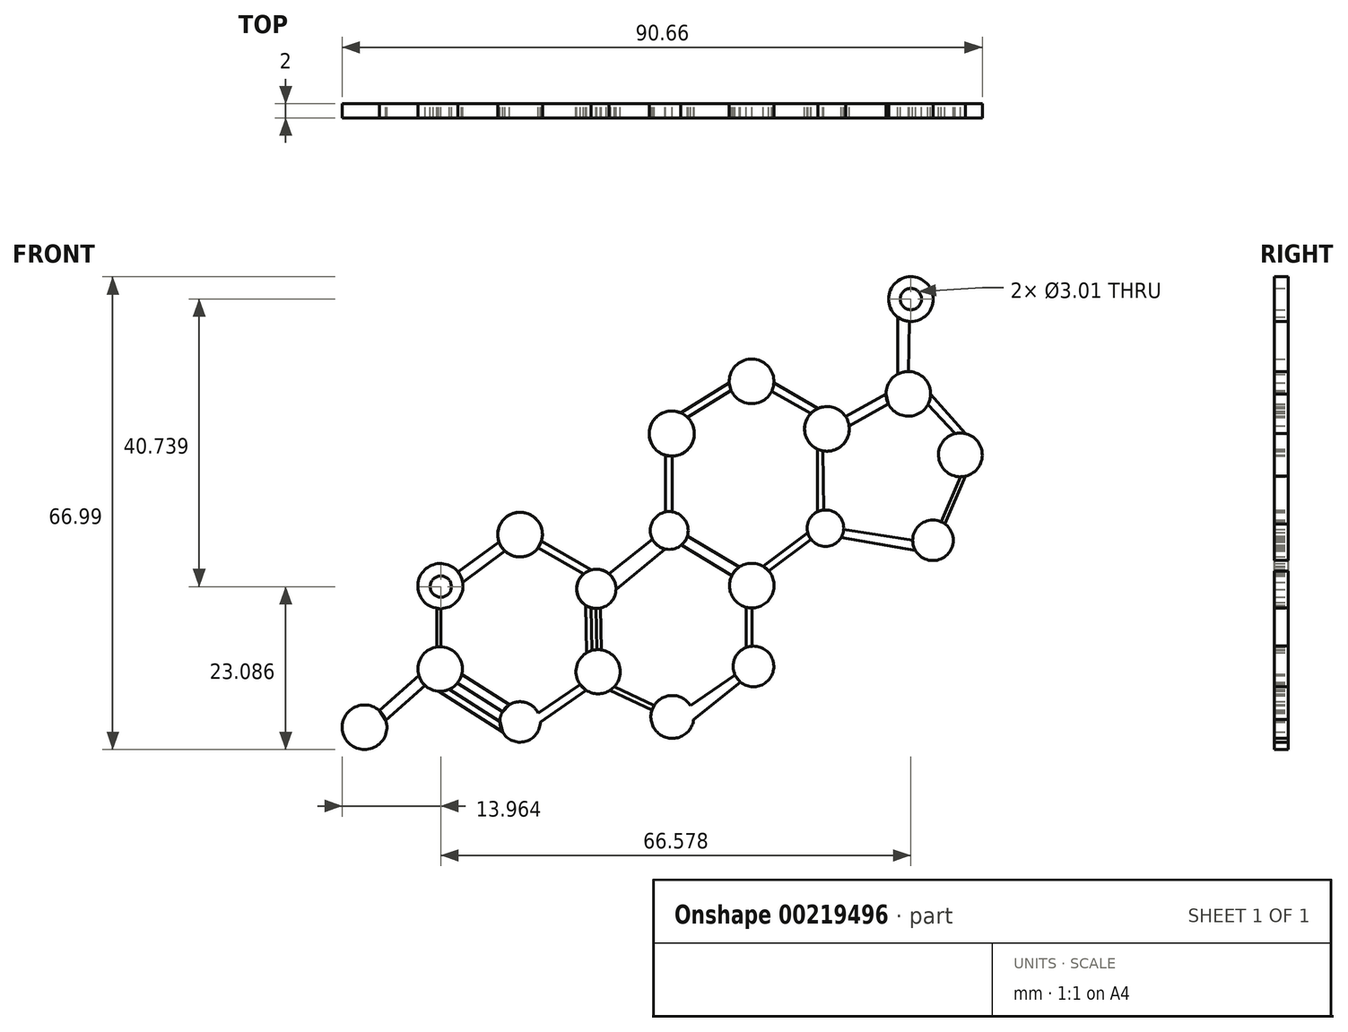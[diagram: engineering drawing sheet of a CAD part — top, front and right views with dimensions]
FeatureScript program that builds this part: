
annotation { "Feature Type Name" : "Feature", "Feature Type Description" : "" }
export const myFeature = defineFeature(function(context is Context, id is Id, definition is map)
    precondition{}
    {
        {
            var Q0;
            Q0=qCreatedBy(makeId("Front.planeOp"),FACE);
            var sketch = newSketch(context, id + "F0", { "sketchPlane" : qUnion([Q0])});
            skCircle(sketch, "E0", {"center": v(-62.79, -30.39) * mm, "radius": 3.16 * mm});
            skCircle(sketch, "E1", {"center": v(-52.09, -22.14) * mm, "radius": 3.15 * mm});
            skCircle(sketch, "E2", {"center": v(-40.76, -29.64) * mm, "radius": 2.86 * mm});
            skCircle(sketch, "E3", {"center": v(-29.71, -22.52) * mm, "radius": 3.13 * mm});
            skCircle(sketch, "E4", {"center": v(-29.95, -10.78) * mm, "radius": 2.78 * mm});
            skCircle(sketch, "E5", {"center": v(-52.05, -10.39) * mm, "radius": 3.2 * mm});
            skCircle(sketch, "E6", {"center": v(-40.75, -3.1) * mm, "radius": 3.16 * mm});
            skCircle(sketch, "E7", {"center": v(-19.19, -28.93) * mm, "radius": 3.04 * mm});
            skCircle(sketch, "E8", {"center": v(-7.7, -21.77) * mm, "radius": 2.88 * mm});
            skCircle(sketch, "E9", {"center": v(-7.93, -10.32) * mm, "radius": 3.16 * mm});
            skCircle(sketch, "E10", {"center": v(-19.63, -2.51) * mm, "radius": 2.68 * mm});
            skCircle(sketch, "E11", {"center": v(2.5, -2.18) * mm, "radius": 2.58 * mm});
            skCircle(sketch, "E12", {"center": v(2.7, 11.88) * mm, "radius": 3.16 * mm});
            skCircle(sketch, "E13", {"center": v(-19.27, 11.22) * mm, "radius": 3.2 * mm});
            skCircle(sketch, "E14", {"center": v(-7.96, 18.61) * mm, "radius": 3.16 * mm});
            skCircle(sketch, "E15", {"center": v(17.72, -3.9) * mm, "radius": 2.87 * mm});
            skCircle(sketch, "E16", {"center": v(21.6, 8.2) * mm, "radius": 3.1 * mm});
            skCircle(sketch, "E17", {"center": v(14.23, 16.85) * mm, "radius": 3.16 * mm});
            skCircle(sketch, "E18", {"center": v(14.6, 30.28) * mm, "radius": 3.16 * mm});
            skLineSegment(sketch, "E19", {"start": v(-51.95, -13.58) * mm, "end": v(-51.95, -18.99) * mm});
            skLineSegment(sketch, "E20", {"start": v(-37.9, -29.64) * mm, "end": v(-31.39, -25.16) * mm});
            skLineSegment(sketch, "E21", {"start": v(-38.2, -4.96) * mm, "end": v(-31.76, -8.67) * mm});
            skLineSegment(sketch, "E22", {"start": v(-28.14, -8.67) * mm, "end": v(-22, -3.76) * mm});
            skLineSegment(sketch, "E23", {"start": v(-7.93, -13.48) * mm, "end": v(-7.93, -18.9) * mm});
            skLineSegment(sketch, "E24", {"start": v(-9.53, -23.99) * mm, "end": v(-16.17, -29.29) * mm});
            skLineSegment(sketch, "E25", {"start": v(-28.04, -25.16) * mm, "end": v(-22.06, -27.94) * mm});
            skLineSegment(sketch, "E26", {"start": v(-19.23, 8.02) * mm, "end": v(-19.23, 0.14) * mm});
            skLineSegment(sketch, "E27", {"start": v(-17.07, 13.53) * mm, "end": v(-10.86, 17.34) * mm});
            skLineSegment(sketch, "E28", {"start": v(-6.33, -7.59) * mm, "end": v(0, -2.8) * mm});
            skLineSegment(sketch, "E29", {"start": v(2.14, 8.77) * mm, "end": v(2.27, 0.39) * mm});
            skLineSegment(sketch, "E30", {"start": v(5.34, 13.63) * mm, "end": v(11.06, 16.85) * mm});
            skLineSegment(sketch, "E31", {"start": v(17.01, 15.35) * mm, "end": v(20.88, 11.22) * mm});
            skLineSegment(sketch, "E32", {"start": v(14.36, 27.12) * mm, "end": v(14.23, 20.01) * mm});
            skLineSegment(sketch, "E33", {"start": v(5.07, -2.37) * mm, "end": v(14.85, -3.9) * mm});
            skLineSegment(sketch, "E34", {"start": v(21.6, 5.1) * mm, "end": v(18.87, -1.27) * mm});
            skLineSegment(sketch, "E35", {"start": v(-50.79, -25) * mm, "end": v(-43.62, -29.58) * mm});
            skLineSegment(sketch, "E36", {"start": v(-49.64, -24.12) * mm, "end": v(-43.24, -28.2) * mm});
            skLineSegment(sketch, "E37", {"start": v(-48.9, -9.85) * mm, "end": v(-42.9, -5.42) * mm});
            skPoint(sketch, "E38.startSnap0", {"position": v(-45.9, -7.63) * mm});
            skLineSegment(sketch, "E39", {"start": v(-49.54, -8.4) * mm, "end": v(-43.75, -4.12) * mm});
            skLineSegment(sketch, "E40", {"start": v(-59.78, -29.4) * mm, "end": v(-54.2, -24.48) * mm});
            skLineSegment(sketch, "E41", {"start": v(-55.1, -23.07) * mm, "end": v(-60.7, -28.01) * mm});
            skLineSegment(sketch, "E42", {"start": v(-59.78, -29.4) * mm, "end": v(-60.7, -28.01) * mm});
            skLineSegment(sketch, "E43", {"start": v(12.7, 19.62) * mm, "end": v(12.7, 27.74) * mm});
            skLineSegment(sketch, "E44", {"start": v(-28.56, -13.19) * mm, "end": v(-27.93, -12.7) * mm});
            skLineSegment(sketch, "E45", {"start": v(-43.24, -28.2) * mm, "end": v(-42.27, -27.2) * mm});
            skLineSegment(sketch, "E46", {"start": v(-42.27, -27.2) * mm, "end": v(-49.03, -22.9) * mm});
            skLineSegment(sketch, "E47", {"start": v(-43.24, -31.06) * mm, "end": v(-52.3, -25.28) * mm});
            skLineSegment(sketch, "E48", {"start": v(-43.62, -29.58) * mm, "end": v(-43.24, -31.06) * mm});
            skLineSegment(sketch, "E49", {"start": v(-38.17, -28.41) * mm, "end": v(-32.25, -24.35) * mm});
            skLineSegment(sketch, "E50", {"start": v(-31.39, -25.16) * mm, "end": v(-32.25, -24.35) * mm});
            skLineSegment(sketch, "E51", {"start": v(-21.76, -27.3) * mm, "end": v(-27.43, -24.67) * mm});
            skLineSegment(sketch, "E52", {"start": v(-28.04, -25.16) * mm, "end": v(-27.43, -24.67) * mm});
            skLineSegment(sketch, "E53", {"start": v(-21.76, -27.3) * mm, "end": v(-22.06, -27.94) * mm});
            skLineSegment(sketch, "E54", {"start": v(-16.6, -27.32) * mm, "end": v(-10.3, -23) * mm});
            skLineSegment(sketch, "E55", {"start": v(-10.3, -23) * mm, "end": v(-9.53, -23.99) * mm});
            skLineSegment(sketch, "E56", {"start": v(-8.73, -19.09) * mm, "end": v(-8.73, -13.38) * mm});
            skLineSegment(sketch, "E57", {"start": v(-8.73, -13.38) * mm, "end": v(-7.93, -13.48) * mm});
            skLineSegment(sketch, "E58", {"start": v(-8.73, -19.09) * mm, "end": v(-7.93, -18.9) * mm});
            skLineSegment(sketch, "E59", {"start": v(-5.53, -8.26) * mm, "end": v(0.45, -3.75) * mm});
            skLineSegment(sketch, "E60", {"start": v(-5.53, -8.26) * mm, "end": v(-6.33, -7.59) * mm});
            skLineSegment(sketch, "E61", {"start": v(-51.95, -13.58) * mm, "end": v(-53.08, -13.4) * mm});
            skLineSegment(sketch, "E62", {"start": v(-37.73, -4.04) * mm, "end": v(-30.68, -8.1) * mm});
            skLineSegment(sketch, "E63", {"start": v(-31.76, -8.67) * mm, "end": v(-38.2, -4.96) * mm});
            skLineSegment(sketch, "E64", {"start": v(-37.73, -4.04) * mm, "end": v(-38.2, -4.96) * mm});
            skLineSegment(sketch, "E65", {"start": v(-20.17, 8.15) * mm, "end": v(-20.17, 0.14) * mm});
            skLineSegment(sketch, "E66", {"start": v(-20.17, 0.14) * mm, "end": v(-19.8, 0.16) * mm});
            skLineSegment(sketch, "E67", {"start": v(-20.17, 8.15) * mm, "end": v(-19.23, 8.02) * mm});
            skLineSegment(sketch, "E68", {"start": v(-18.04, 14.17) * mm, "end": v(-11.12, 18.41) * mm});
            skLineSegment(sketch, "E69", {"start": v(-11.12, 18.41) * mm, "end": v(-10.86, 17.34) * mm});
            skLineSegment(sketch, "E70", {"start": v(1.37, 9.01) * mm, "end": v(1.37, 0.14) * mm});
            skLineSegment(sketch, "E71", {"start": v(2.14, 8.77) * mm, "end": v(1.37, 9.01) * mm});
            skLineSegment(sketch, "E72", {"start": v(5.84, 12.29) * mm, "end": v(11.4, 15.41) * mm});
            skLineSegment(sketch, "E73", {"start": v(11.4, 15.41) * mm, "end": v(11.06, 16.85) * mm});
            skLineSegment(sketch, "E74", {"start": v(17.4, 16.85) * mm, "end": v(22.33, 11.22) * mm});
            skPoint(sketch, "E75.endSnap0", {"position": v(19.86, 14.03) * mm});
            skLineSegment(sketch, "E76", {"start": v(21.6, 5.1) * mm, "end": v(22.33, 5.18) * mm});
            skLineSegment(sketch, "E77", {"start": v(4.7, -3.53) * mm, "end": v(15.24, -5.35) * mm});
            skLineSegment(sketch, "E78", {"start": v(-27.17, -10.89) * mm, "end": v(-20.2, -5.13) * mm});
            skLineSegment(sketch, "E79", {"start": v(-17.9, -4.57) * mm, "end": v(-10.75, -8.87) * mm});
            skLineSegment(sketch, "E80", {"start": v(-17.06, -3.28) * mm, "end": v(-9.71, -7.7) * mm});
            skLineSegment(sketch, "E81", {"start": v(-31.47, -13.1) * mm, "end": v(-31.32, -19.84) * mm});
            skLineSegment(sketch, "E82", {"start": v(-30.68, -13.47) * mm, "end": v(-30.59, -19.52) * mm});
            skLineSegment(sketch, "E83", {"start": v(-29.98, -13.56) * mm, "end": v(-29.89, -19.4) * mm});
            skLineSegment(sketch, "E84", {"start": v(-29.35, -13.5) * mm, "end": v(-29.26, -19.42) * mm});
            skLineSegment(sketch, "E85", {"start": v(-52.51, -13.5) * mm, "end": v(-52.51, -19.01) * mm});
            skLineSegment(sketch, "E86", {"start": v(-4.8, 18.43) * mm, "end": v(1.41, 14.77) * mm});
            skLineSegment(sketch, "E87", {"start": v(-5.3, 17.28) * mm, "end": v(0.43, 14.07) * mm});
            skLineSegment(sketch, "E88", {"start": v(22.33, 5.18) * mm, "end": v(19.43, -1.59) * mm});
            skCircle(sketch, "E89", {"center": v(14.6, 30.28) * mm, "radius": 1.5 * mm});
            skCircle(sketch, "E90", {"center": v(-51.99, -10.46) * mm, "radius": 1.5 * mm});
            skSolve(sketch);
        }
        {
            var Q0;
            {var subQ3=sQuery(id+"F0.wireOp",EDGE,"E64");Q0=makeQuery(id+"F0.imprint","IMPRINT",FACE,{"disambiguationData":[TD([[makeQuery(id+"F0.imprint","IMPRINT",EDGE,{"derivedFrom":subQ3}),-1.0]])]});}
            var Q1;
            {var subQ0=sQuery(id+"F0.wireOp",EDGE,"Mb7MF2RT-jddo-B6ze-xgIj-n0XcXyZHC1Ex");Q1=makeQuery(id+"F0.imprint","IMPRINT",FACE,{"disambiguationData":[TD([[makeQuery(id+"F0.imprint","IMPRINT",EDGE,{"derivedFrom":subQ0}),1.0]])]});}
            var Q2;
            {var subQ1=sQuery(id+"F0.wireOp",EDGE,"E37");Q2=makeQuery(id+"F0.imprint","IMPRINT",FACE,{"disambiguationData":[TD([[makeQuery(id+"F0.imprint","IMPRINT",EDGE,{"derivedFrom":subQ1}),1.0]])]});}
            var Q3;
            {var subQ1=sQuery(id+"F0.wireOp",EDGE,"E19");Q3=makeQuery(id+"F0.imprint","IMPRINT",FACE,{"disambiguationData":[TD([[makeQuery(id+"F0.imprint","IMPRINT",EDGE,{"derivedFrom":subQ1}),-1.0]])]});}
            var Q4;
            {var subQ5=sQuery(id+"F0.wireOp",EDGE,"a1dBgSWb-6DuU-worO-kKtV-IeXW11xfBRhP");Q4=makeQuery(id+"F0.imprint","IMPRINT",FACE,{"disambiguationData":[TD([[makeQuery(id+"F0.imprint","IMPRINT",EDGE,{"derivedFrom":subQ5}),-1.0]])]});}
            var Q5;
            {var subQ1=sQuery(id+"F0.wireOp",EDGE,"E40");Q5=makeQuery(id+"F0.imprint","IMPRINT",FACE,{"disambiguationData":[TD([[makeQuery(id+"F0.imprint","IMPRINT",EDGE,{"derivedFrom":subQ1}),1.0]])]});}
            var Q6;
            {var subQ0=sQuery(id+"F0.wireOp",EDGE,"E42");Q6=makeQuery(id+"F0.imprint","IMPRINT",FACE,{"disambiguationData":[TD([[makeQuery(id+"F0.imprint","IMPRINT",EDGE,{"derivedFrom":subQ0}),1.0]])]});}
            var Q7;
            {var subQ1=sQuery(id+"F0.wireOp",EDGE,"E36");Q7=makeQuery(id+"F0.imprint","IMPRINT",FACE,{"disambiguationData":[TD([[makeQuery(id+"F0.imprint","IMPRINT",EDGE,{"derivedFrom":subQ1}),1.0]])]});}
            var Q8;
            {var subQ1=sQuery(id+"F0.wireOp",EDGE,"E35");Q8=makeQuery(id+"F0.imprint","IMPRINT",FACE,{"disambiguationData":[TD([[makeQuery(id+"F0.imprint","IMPRINT",EDGE,{"derivedFrom":subQ1}),-1.0]])]});}
            var Q9;
            {var subQ1=sQuery(id+"F0.wireOp",EDGE,"E20");Q9=makeQuery(id+"F0.imprint","IMPRINT",FACE,{"disambiguationData":[TD([[makeQuery(id+"F0.imprint","IMPRINT",EDGE,{"derivedFrom":subQ1}),1.0]])]});}
            var Q10;
            {var subQ3=sQuery(id+"F0.wireOp",EDGE,"E45");Q10=makeQuery(id+"F0.imprint","IMPRINT",FACE,{"disambiguationData":[TD([[makeQuery(id+"F0.imprint","IMPRINT",EDGE,{"derivedFrom":subQ3}),-1.0]])]});}
            var Q11;
            {var subQ0=sQuery(id+"F0.wireOp",EDGE,"E50");Q11=makeQuery(id+"F0.imprint","IMPRINT",FACE,{"disambiguationData":[TD([[makeQuery(id+"F0.imprint","IMPRINT",EDGE,{"derivedFrom":subQ0}),-1.0]])]});}
            var Q12;
            Q12=makeQuery(id+"F0.imprint","IMPRINT",FACE,{"disambiguationData":[TD([[makeQuery(id+"F0.imprint","IMPRINT",EDGE,{"derivedFrom":sQuery(id+"F0.wireOp",EDGE,"5VwYfp6s-fnZS-L74V-JAx9-Tji8LIlleJzu.bottom")}),-1.0]])]});
            var Q13;
            {var subQ5=sQuery(id+"F0.wireOp",EDGE,"M7uNgQcp-6DOX-0CdO-FolA-AVuqSKqm1bxD.bottom");Q13=makeQuery(id+"F0.imprint","IMPRINT",FACE,{"disambiguationData":[TD([[makeQuery(id+"F0.imprint","IMPRINT",EDGE,{"derivedFrom":subQ5}),-1.0]])]});}
            var Q14;
            {var subQ0=sQuery(id+"F0.wireOp",EDGE,"E44");Q14=makeQuery(id+"F0.imprint","IMPRINT",FACE,{"disambiguationData":[TD([[makeQuery(id+"F0.imprint","IMPRINT",EDGE,{"derivedFrom":subQ0}),1.0]])]});}
            var Q15;
            {var subQ0=sQuery(id+"F0.wireOp",EDGE,"E62");Q15=makeQuery(id+"F0.imprint","IMPRINT",FACE,{"disambiguationData":[TD([[makeQuery(id+"F0.imprint","IMPRINT",EDGE,{"derivedFrom":subQ0}),-1.0]])]});}
            var Q16;
            {var subQ1=sQuery(id+"F0.wireOp",EDGE,"E22");Q16=makeQuery(id+"F0.imprint","IMPRINT",FACE,{"disambiguationData":[TD([[makeQuery(id+"F0.imprint","IMPRINT",EDGE,{"derivedFrom":subQ1}),-1.0]])]});}
            var Q17;
            {var subQ0=sQuery(id+"F0.wireOp",EDGE,"UeHGOHKe-4UKH-cGRf-4B86-QE9oBGHCOTL0");Q17=makeQuery(id+"F0.imprint","IMPRINT",FACE,{"disambiguationData":[TD([[makeQuery(id+"F0.imprint","IMPRINT",EDGE,{"derivedFrom":subQ0}),1.0]])]});}
            var Q18;
            {var subQ1=sQuery(id+"F0.wireOp",EDGE,"E25");Q18=makeQuery(id+"F0.imprint","IMPRINT",FACE,{"disambiguationData":[TD([[makeQuery(id+"F0.imprint","IMPRINT",EDGE,{"derivedFrom":subQ1}),1.0]])]});}
            var Q19;
            {var subQ0=sQuery(id+"F0.wireOp",EDGE,"E53");Q19=makeQuery(id+"F0.imprint","IMPRINT",FACE,{"disambiguationData":[TD([[makeQuery(id+"F0.imprint","IMPRINT",EDGE,{"derivedFrom":subQ0}),1.0]])]});}
            var Q20;
            {var subQ1=sQuery(id+"F0.wireOp",EDGE,"E24");Q20=makeQuery(id+"F0.imprint","IMPRINT",FACE,{"disambiguationData":[TD([[makeQuery(id+"F0.imprint","IMPRINT",EDGE,{"derivedFrom":subQ1}),-1.0]])]});}
            var Q21;
            {var subQ0=sQuery(id+"F0.wireOp",EDGE,"E55");Q21=makeQuery(id+"F0.imprint","IMPRINT",FACE,{"disambiguationData":[TD([[makeQuery(id+"F0.imprint","IMPRINT",EDGE,{"derivedFrom":subQ0}),1.0]])]});}
            var Q22;
            {var subQ1=sQuery(id+"F0.wireOp",EDGE,"E23");Q22=makeQuery(id+"F0.imprint","IMPRINT",FACE,{"disambiguationData":[TD([[makeQuery(id+"F0.imprint","IMPRINT",EDGE,{"derivedFrom":subQ1}),-1.0]])]});}
            var Q23;
            {var subQ0=sQuery(id+"F0.wireOp",EDGE,"E57");Q23=makeQuery(id+"F0.imprint","IMPRINT",FACE,{"disambiguationData":[TD([[makeQuery(id+"F0.imprint","IMPRINT",EDGE,{"derivedFrom":subQ0}),1.0]])]});}
            var Q24;
            {var subQ1=sQuery(id+"F0.wireOp",EDGE,"E28");Q24=makeQuery(id+"F0.imprint","IMPRINT",FACE,{"disambiguationData":[TD([[makeQuery(id+"F0.imprint","IMPRINT",EDGE,{"derivedFrom":subQ1}),-1.0]])]});}
            var Q25;
            {var subQ0=sQuery(id+"F0.wireOp",EDGE,"Ezyj9Kgh-BWDU-0eJ4-APll-MsjRslF86DpF");Q25=makeQuery(id+"F0.imprint","IMPRINT",FACE,{"disambiguationData":[TD([[makeQuery(id+"F0.imprint","IMPRINT",EDGE,{"derivedFrom":subQ0}),-1.0]])]});}
            var Q26;
            {var subQ1=sQuery(id+"F0.wireOp",EDGE,"E29");Q26=makeQuery(id+"F0.imprint","IMPRINT",FACE,{"disambiguationData":[TD([[makeQuery(id+"F0.imprint","IMPRINT",EDGE,{"derivedFrom":subQ1}),-1.0]])]});}
            var Q27;
            {var subQ0=sQuery(id+"F0.wireOp",EDGE,"E71");Q27=makeQuery(id+"F0.imprint","IMPRINT",FACE,{"disambiguationData":[TD([[makeQuery(id+"F0.imprint","IMPRINT",EDGE,{"derivedFrom":subQ0}),-1.0]])]});}
            var Q28;
            {var subQ0=sQuery(id+"F0.wireOp",EDGE,"sSouhH1C-a7Wg-rKGi-7Wp8-vkzoGwjJmSID");Q28=makeQuery(id+"F0.imprint","IMPRINT",FACE,{"disambiguationData":[TD([[makeQuery(id+"F0.imprint","IMPRINT",EDGE,{"derivedFrom":subQ0}),-1.0]])]});}
            var Q29;
            {var subQ1=sQuery(id+"F0.wireOp",EDGE,"vSaMkwXp-oE9S-KJV4-mMeU-YnlZ7d6mE9Y9");Q29=makeQuery(id+"F0.imprint","IMPRINT",FACE,{"disambiguationData":[TD([[makeQuery(id+"F0.imprint","IMPRINT",EDGE,{"derivedFrom":subQ1}),-1.0]])]});}
            var Q30;
            {var subQ0=sQuery(id+"F0.wireOp",EDGE,"E68");Q30=makeQuery(id+"F0.imprint","IMPRINT",FACE,{"disambiguationData":[TD([[makeQuery(id+"F0.imprint","IMPRINT",EDGE,{"derivedFrom":subQ0}),-1.0]])]});}
            var Q31;
            {var subQ0=sQuery(id+"F0.wireOp",EDGE,"E67");Q31=makeQuery(id+"F0.imprint","IMPRINT",FACE,{"disambiguationData":[TD([[makeQuery(id+"F0.imprint","IMPRINT",EDGE,{"derivedFrom":subQ0}),1.0]])]});}
            var Q32;
            {var subQ4=sQuery(id+"F0.wireOp",EDGE,"E65");Q32=makeQuery(id+"F0.imprint","IMPRINT",FACE,{"disambiguationData":[TD([[makeQuery(id+"F0.imprint","IMPRINT",EDGE,{"derivedFrom":subQ4}),1.0]])]});}
            var Q33;
            {var subQ1=sQuery(id+"F0.wireOp",EDGE,"E30");Q33=makeQuery(id+"F0.imprint","IMPRINT",FACE,{"disambiguationData":[TD([[makeQuery(id+"F0.imprint","IMPRINT",EDGE,{"derivedFrom":subQ1}),-1.0]])]});}
            var Q34;
            {var subQ1=sQuery(id+"F0.wireOp",EDGE,"E32");Q34=makeQuery(id+"F0.imprint","IMPRINT",FACE,{"disambiguationData":[TD([[makeQuery(id+"F0.imprint","IMPRINT",EDGE,{"derivedFrom":subQ1}),-1.0]])]});}
            var Q35;
            {var subQ0=sQuery(id+"F0.wireOp",EDGE,"sPN0vxyv-kXMr-WsTe-n2yW-GJKV4UbPOXA4");Q35=makeQuery(id+"F0.imprint","IMPRINT",FACE,{"disambiguationData":[TD([[makeQuery(id+"F0.imprint","IMPRINT",EDGE,{"derivedFrom":subQ0}),-1.0]])]});}
            var Q36;
            {var subQ0=sQuery(id+"F0.wireOp",EDGE,"IRrBQA8b-qcgg-vGCc-qcpc-6L5ACvAlk9N0");Q36=makeQuery(id+"F0.imprint","IMPRINT",FACE,{"disambiguationData":[TD([[makeQuery(id+"F0.imprint","IMPRINT",EDGE,{"derivedFrom":subQ0}),-1.0]])]});}
            var Q37;
            {var subQ1=sQuery(id+"F0.wireOp",EDGE,"E31");Q37=makeQuery(id+"F0.imprint","IMPRINT",FACE,{"disambiguationData":[TD([[makeQuery(id+"F0.imprint","IMPRINT",EDGE,{"derivedFrom":subQ1}),1.0]])]});}
            var Q38;
            {var subQ0=sQuery(id+"F0.wireOp",EDGE,"uFY3qbvF-FtAH-bahm-cErt-nJcObRJHhIVn");Q38=makeQuery(id+"F0.imprint","IMPRINT",FACE,{"disambiguationData":[TD([[makeQuery(id+"F0.imprint","IMPRINT",EDGE,{"derivedFrom":subQ0}),1.0]])]});}
            var Q39;
            {var subQ1=sQuery(id+"F0.wireOp",EDGE,"E34");Q39=makeQuery(id+"F0.imprint","IMPRINT",FACE,{"disambiguationData":[TD([[makeQuery(id+"F0.imprint","IMPRINT",EDGE,{"derivedFrom":subQ1}),1.0]])]});}
            var Q40;
            {var subQ0=sQuery(id+"F0.wireOp",EDGE,"sUYJAU2J-VXak-0DQV-njkR-GLYZazPf4Nhu");Q40=makeQuery(id+"F0.imprint","IMPRINT",FACE,{"disambiguationData":[TD([[makeQuery(id+"F0.imprint","IMPRINT",EDGE,{"derivedFrom":subQ0}),-1.0]])]});}
            var Q41;
            {var subQ1=sQuery(id+"F0.wireOp",EDGE,"E33");Q41=makeQuery(id+"F0.imprint","IMPRINT",FACE,{"disambiguationData":[TD([[makeQuery(id+"F0.imprint","IMPRINT",EDGE,{"derivedFrom":subQ1}),-1.0]])]});}
            extrude(context, id + "F1", {"entities" : qUnion([Q0, Q1, Q2, Q3, Q4, Q5, Q6, Q7, Q8, Q9, Q10, Q11, Q12, Q13, Q14, Q15, Q16, Q17, Q18, Q19, Q20, Q21, Q22, Q23, Q24, Q25, Q26, Q27, Q28, Q29, Q30, Q31, Q32, Q33, Q34, Q35, Q36, Q37, Q38, Q39, Q40, Q41]), "depth" : 2 * mm});
        }
        {
            var Q0;
            {var subQ1=sQuery(id+"F0.wireOp",EDGE,"E79");Q0=makeQuery(id+"F0.imprint","IMPRINT",FACE,{"disambiguationData":[TD([[makeQuery(id+"F0.imprint","IMPRINT",EDGE,{"derivedFrom":subQ1}),1.0]])]});}
            extrude(context, id + "F2", {"entities" : qUnion([Q0]), "depth" : 2 * mm});
        }
        {
            var Q0;
            {var subQ1=sQuery(id+"F0.wireOp",EDGE,"E22");Q0=makeQuery(id+"F0.imprint","IMPRINT",FACE,{"disambiguationData":[TD([[makeQuery(id+"F0.imprint","IMPRINT",EDGE,{"derivedFrom":subQ1}),-1.0]])]});}
            extrude(context, id + "F3", {"entities" : qUnion([Q0]), "depth" : 2 * mm});
        }
        {
            var Q0;
            {var subQ0=sQuery(id+"F0.wireOp",EDGE,"E81");Q0=makeQuery(id+"F0.imprint","IMPRINT",FACE,{"disambiguationData":[TD([[makeQuery(id+"F0.imprint","IMPRINT",EDGE,{"derivedFrom":subQ0}),1.0]])]});}
            extrude(context, id + "F4", {"entities" : qUnion([Q0]), "depth" : 2 * mm});
        }
        {
            var Q0;
            {var subQ0=sQuery(id+"F0.wireOp",EDGE,"E22");Q0=makeQuery(id+"F0.imprint","IMPRINT",FACE,{"disambiguationData":[TD([[makeQuery(id+"F0.imprint","IMPRINT",EDGE,{"derivedFrom":subQ0}),-1.0]])]});}
            var Q1;
            {var subQ0=sQuery(id+"F0.wireOp",EDGE,"E83");Q1=makeQuery(id+"F0.imprint","IMPRINT",FACE,{"disambiguationData":[TD([[makeQuery(id+"F0.imprint","IMPRINT",EDGE,{"derivedFrom":subQ0}),1.0]])]});}
            extrude(context, id + "F5", {"entities" : qUnion([Q0, Q1]), "depth" : 2 * mm});
        }
        {
            var Q0;
            {var subQ3=sQuery(id+"F0.wireOp",EDGE,"E64");Q0=makeQuery(id+"F0.imprint","IMPRINT",FACE,{"disambiguationData":[TD([[makeQuery(id+"F0.imprint","IMPRINT",EDGE,{"derivedFrom":subQ3}),-1.0]])]});}
            var Q1;
            {var subQ1=sQuery(id+"F0.wireOp",EDGE,"E5");var subQ4=makeQuery(id+"F0.imprint","INTERSECT",VERTEX,{"derivedFrom":[subQ1,sQuery(id+"F0.wireOp",EDGE,"E37")]});Q1=makeQuery(id+"F0.imprint","IMPRINT",FACE,{"disambiguationData":[TD([[makeQuery(id+"F0.imprint","IMPRINT",EDGE,{"disambiguationData":[TD([[subQ4,-1.0]])],"derivedFrom":subQ1}),1.0]])]});}
            var Q2;
            {var subQ7=sQuery(id+"F0.wireOp",EDGE,"E44");Q2=makeQuery(id+"F0.imprint","IMPRINT",FACE,{"disambiguationData":[TD([[makeQuery(id+"F0.imprint","IMPRINT",EDGE,{"derivedFrom":subQ7}),1.0]])]});}
            var Q3;
            {var subQ0=sQuery(id+"F0.wireOp",EDGE,"E22");Q3=makeQuery(id+"F0.imprint","IMPRINT",FACE,{"disambiguationData":[TD([[makeQuery(id+"F0.imprint","IMPRINT",EDGE,{"derivedFrom":subQ0}),-1.0]])]});}
            var Q4;
            {var subQ3=sQuery(id+"F0.wireOp",EDGE,"E67");Q4=makeQuery(id+"F0.imprint","IMPRINT",FACE,{"disambiguationData":[TD([[makeQuery(id+"F0.imprint","IMPRINT",EDGE,{"derivedFrom":subQ3}),1.0]])]});}
            var Q5;
            {var subQ0=sQuery(id+"F0.wireOp",EDGE,"E69");Q5=makeQuery(id+"F0.imprint","IMPRINT",FACE,{"disambiguationData":[TD([[makeQuery(id+"F0.imprint","IMPRINT",EDGE,{"derivedFrom":subQ0}),1.0]])]});}
            var Q6;
            {var subQ0=sQuery(id+"F0.wireOp",EDGE,"E11");var subQ5=makeQuery(id+"F0.imprint","INTERSECT",VERTEX,{"derivedFrom":[subQ0,sQuery(id+"F0.wireOp",EDGE,"E29")]});Q6=makeQuery(id+"F0.imprint","IMPRINT",FACE,{"disambiguationData":[TD([[makeQuery(id+"F0.imprint","IMPRINT",EDGE,{"disambiguationData":[TD([[subQ5,-1.0]])],"derivedFrom":subQ0}),1.0]])]});}
            var Q7;
            {var subQ0=sQuery(id+"F0.wireOp",EDGE,"E71");Q7=makeQuery(id+"F0.imprint","IMPRINT",FACE,{"disambiguationData":[TD([[makeQuery(id+"F0.imprint","IMPRINT",EDGE,{"derivedFrom":subQ0}),-1.0]])]});}
            extrude(context, id + "F6", {"entities" : qUnion([Q0, Q1, Q2, Q3, Q4, Q5, Q6, Q7]), "depth" : 2 * mm});
        }
        {
            var Q0;
            {var subQ0=sQuery(id+"F0.wireOp",EDGE,"E1");var subQ5=makeQuery(id+"F0.imprint","INTERSECT",VERTEX,{"derivedFrom":[subQ0,sQuery(id+"F0.wireOp",EDGE,"E19")]});Q0=makeQuery(id+"F0.imprint","IMPRINT",FACE,{"disambiguationData":[TD([[makeQuery(id+"F0.imprint","IMPRINT",EDGE,{"disambiguationData":[TD([[subQ5,-1.0]])],"derivedFrom":subQ0}),1.0]])]});}
            var Q1;
            {var subQ7=sQuery(id+"F0.wireOp",EDGE,"E44");Q1=makeQuery(id+"F0.imprint","IMPRINT",FACE,{"disambiguationData":[TD([[makeQuery(id+"F0.imprint","IMPRINT",EDGE,{"derivedFrom":subQ7}),1.0]])]});}
            var Q2;
            {var subQ0=sQuery(id+"F0.wireOp",EDGE,"E11");var subQ5=makeQuery(id+"F0.imprint","INTERSECT",VERTEX,{"derivedFrom":[subQ0,sQuery(id+"F0.wireOp",EDGE,"E29")]});Q2=makeQuery(id+"F0.imprint","IMPRINT",FACE,{"disambiguationData":[TD([[makeQuery(id+"F0.imprint","IMPRINT",EDGE,{"disambiguationData":[TD([[subQ5,-1.0]])],"derivedFrom":subQ0}),1.0]])]});}
            var Q3;
            {var subQ0=sQuery(id+"F0.wireOp",EDGE,"E15");var subQ1=makeQuery(id+"F0.imprint","INTERSECT",VERTEX,{"derivedFrom":[subQ0,sQuery(id+"F0.wireOp",EDGE,"E34")]});Q3=makeQuery(id+"F0.imprint","IMPRINT",FACE,{"disambiguationData":[TD([[makeQuery(id+"F0.imprint","IMPRINT",EDGE,{"disambiguationData":[TD([[subQ1,1.0]])],"derivedFrom":subQ0}),1.0]])]});}
            var Q4;
            {var subQ3=sQuery(id+"F0.wireOp",EDGE,"E76");Q4=makeQuery(id+"F0.imprint","IMPRINT",FACE,{"disambiguationData":[TD([[makeQuery(id+"F0.imprint","IMPRINT",EDGE,{"derivedFrom":subQ3}),1.0]])]});}
            var Q5;
            {var subQ3=sQuery(id+"F0.wireOp",EDGE,"E73");Q5=makeQuery(id+"F0.imprint","IMPRINT",FACE,{"disambiguationData":[TD([[makeQuery(id+"F0.imprint","IMPRINT",EDGE,{"derivedFrom":subQ3}),-1.0]])]});}
            var Q6;
            {var subQ0=sQuery(id+"F0.wireOp",EDGE,"E18");var subQ1=makeQuery(id+"F0.imprint","INTERSECT",VERTEX,{"derivedFrom":[subQ0,sQuery(id+"F0.wireOp",EDGE,"E32")]});Q6=makeQuery(id+"F0.imprint","IMPRINT",FACE,{"disambiguationData":[TD([[makeQuery(id+"F0.imprint","IMPRINT",EDGE,{"disambiguationData":[TD([[subQ1,1.0]])],"derivedFrom":subQ0}),1.0]])]});}
            var Q7;
            {var subQ0=sQuery(id+"F0.wireOp",EDGE,"E71");Q7=makeQuery(id+"F0.imprint","IMPRINT",FACE,{"disambiguationData":[TD([[makeQuery(id+"F0.imprint","IMPRINT",EDGE,{"derivedFrom":subQ0}),-1.0]])]});}
            extrude(context, id + "F7", {"entities" : qUnion([Q0, Q1, Q2, Q3, Q4, Q5, Q6, Q7]), "depth" : 2 * mm});
        }
        {
            var Q0;
            {var subQ0=sQuery(id+"F0.wireOp",EDGE,"E10");var subQ5=makeQuery(id+"F0.imprint","INTERSECT",VERTEX,{"derivedFrom":[subQ0,sQuery(id+"F0.wireOp",EDGE,"E26")]});Q0=makeQuery(id+"F0.imprint","IMPRINT",FACE,{"disambiguationData":[TD([[makeQuery(id+"F0.imprint","IMPRINT",EDGE,{"disambiguationData":[TD([[subQ5,-1.0]])],"derivedFrom":subQ0}),1.0]])]});}
            var Q1;
            {var subQ0=sQuery(id+"F0.wireOp",EDGE,"E86");Q1=makeQuery(id+"F0.imprint","IMPRINT",FACE,{"disambiguationData":[TD([[makeQuery(id+"F0.imprint","IMPRINT",EDGE,{"derivedFrom":subQ0}),-1.0]])]});}
            extrude(context, id + "F8", {"entities" : qUnion([Q0, Q1]), "depth" : 2 * mm});
        }
        {
            var Q0;
            {var subQ0=sQuery(id+"F0.wireOp",EDGE,"E37");Q0=makeQuery(id+"F0.imprint","IMPRINT",FACE,{"disambiguationData":[TD([[makeQuery(id+"F0.imprint","IMPRINT",EDGE,{"derivedFrom":subQ0}),1.0]])]});}
            extrude(context, id + "F9", {"entities" : qUnion([Q0]), "depth" : 2 * mm});
        }
    });
